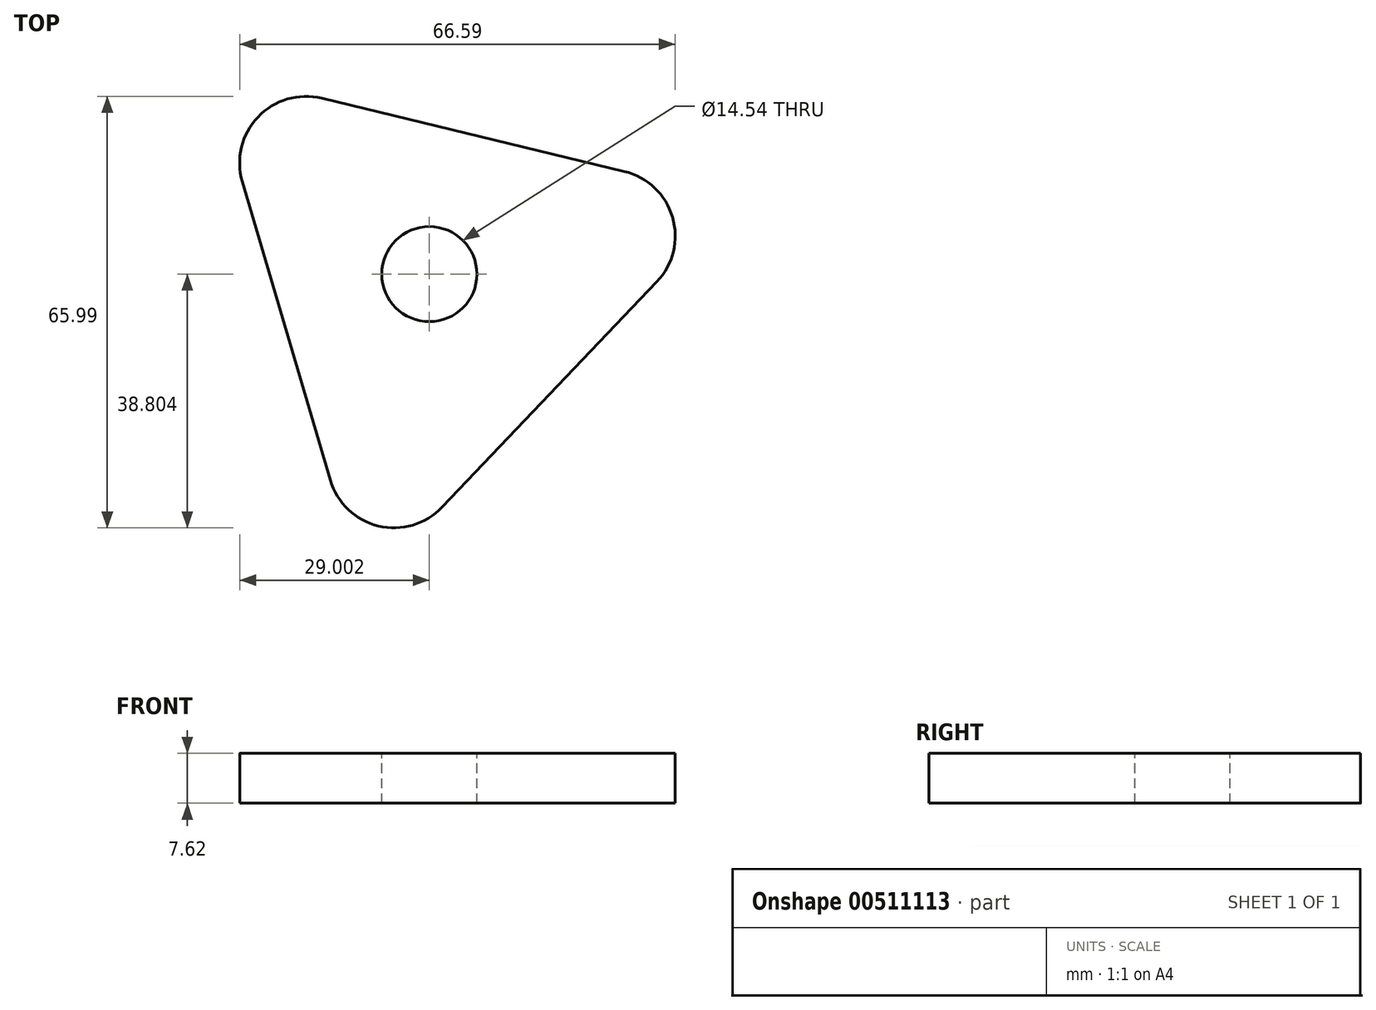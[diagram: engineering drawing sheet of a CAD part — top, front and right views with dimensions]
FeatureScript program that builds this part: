
annotation { "Feature Type Name" : "Feature", "Feature Type Description" : "" }
export const myFeature = defineFeature(function(context is Context, id is Id, definition is map)
    precondition{}
    {
        {
            var Q0;
            Q0=qCreatedBy(makeId("Top.planeOp"),FACE);
            var sketch = newSketch(context, id + "F0", { "sketchPlane" : qUnion([Q0])});
            skLineSegment(sketch, "E0", {"start": v(-31.56, 28.29) * mm, "end": v(-18.12, -17.38) * mm});
            skLineSegment(sketch, "E1", {"start": v(-1.01, -21.52) * mm, "end": v(31.82, 12.96) * mm});
            skLineSegment(sketch, "E2", {"start": v(26.85, 29.84) * mm, "end": v(-19.42, 41.03) * mm});
            skPoint(sketch, "E3.visualSharp", {"position": v(-36.53, 45.17) * mm});
            skArc(sketch, "E3.filletArc", {"start": v(-19.42, 41.03) * mm, "mid": v(-29.17, 38.16) * mm, "end": v(-31.56, 28.29) * mm});
            skPoint(sketch, "E4.visualSharp", {"position": v(-13.15, -34.26) * mm});
            skArc(sketch, "E4.filletArc", {"start": v(-18.12, -17.38) * mm, "mid": v(-10.76, -24.38) * mm, "end": v(-1.01, -21.52) * mm});
            skPoint(sketch, "E5.visualSharp", {"position": v(43.95, 25.7) * mm});
            skArc(sketch, "E5.filletArc", {"start": v(31.82, 12.96) * mm, "mid": v(34.2, 22.83) * mm, "end": v(26.85, 29.84) * mm});
            skSolve(sketch);
        }
        {
            var Q0;
            Q0=makeQuery(id+"F0.imprint","IMPRINT",FACE,{"disambiguationData":[TD([[makeQuery(id+"F0.imprint","IMPRINT",EDGE,{"derivedFrom":sQuery(id+"F0.wireOp",EDGE,"E0")}),1.0]])]});
            extrude(context, id + "F1", {"entities" : qUnion([Q0]), "depth" : 7.62 * mm});
        }
        {
            var Q0;
            Q0=makeQuery(id+"F1.opExtrude","CAP_FACE",FACE,{"disambiguationData":[OSD([sQuery(id+"F0.wireOp",EDGE,"E0"),sQuery(id+"F0.wireOp",EDGE,"E1"),sQuery(id+"F0.wireOp",EDGE,"E2"),sQuery(id+"F0.wireOp",EDGE,"E3.filletArc"),sQuery(id+"F0.wireOp",EDGE,"E4.filletArc"),sQuery(id+"F0.wireOp",EDGE,"E5.filletArc")])],"isStart":false});
            var sketch = newSketch(context, id + "F2", { "sketchPlane" : qUnion([Q0])});
            skCircle(sketch, "E6", {"center": v(-2.97, 14.13) * mm, "radius": 7.27 * mm});
            skSolve(sketch);
        }
        {
            var Q0;
            Q0=makeQuery(id+"F2.imprint","IMPRINT",FACE,{"disambiguationData":[TD([[makeQuery(id+"F2.imprint","IMPRINT",EDGE,{"derivedFrom":sQuery(id+"F2.wireOp",EDGE,"E6")}),1.0]])]});
            extrude(context, id + "F3", {"entities" : qUnion([Q0]), "operationType" : NewBodyOperationType.REMOVE, "oppositeDirection" : true, "depth" : 25.4 * mm});
        }
    });
